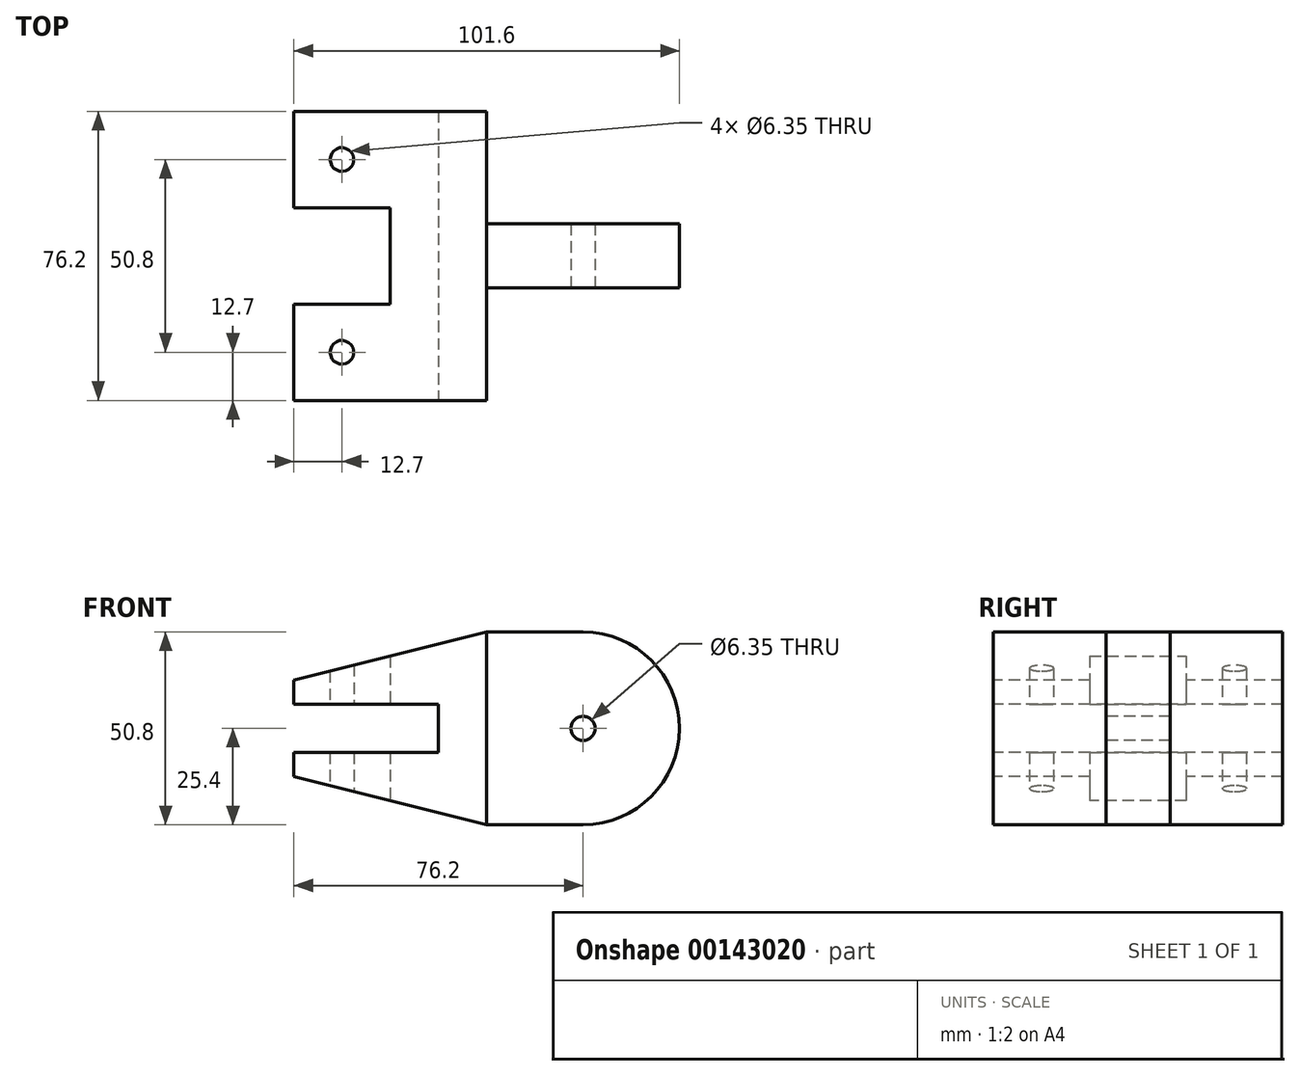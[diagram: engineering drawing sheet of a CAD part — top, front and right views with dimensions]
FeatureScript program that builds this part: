
annotation { "Feature Type Name" : "Feature", "Feature Type Description" : "" }
export const myFeature = defineFeature(function(context is Context, id is Id, definition is map)
    precondition{}
    {
        {
            var Q0;
            Q0=qCreatedBy(makeId("Top.planeOp"),FACE);
            var sketch = newSketch(context, id + "F0", { "sketchPlane" : qUnion([Q0])});
            skLineSegment(sketch, "E0.bottom", {"start": v(0, 0) * mm, "end": v(-50.8, 0) * mm});
            skLineSegment(sketch, "E0.top", {"start": v(0, 76.2) * mm, "end": v(-50.8, 76.2) * mm});
            skLineSegment(sketch, "E0.left", {"start": v(0, 0) * mm, "end": v(0, 76.2) * mm});
            skLineSegment(sketch, "E0.right", {"start": v(-50.8, 0) * mm, "end": v(-50.8, 25.4) * mm});
            skLineSegment(sketch, "E1.bottom", {"start": v(-50.8, 50.8) * mm, "end": v(-25.4, 50.8) * mm});
            skLineSegment(sketch, "E1.top", {"start": v(-50.8, 25.4) * mm, "end": v(-25.4, 25.4) * mm});
            skLineSegment(sketch, "E1.right", {"start": v(-25.4, 50.8) * mm, "end": v(-25.4, 25.4) * mm});
            skLineSegment(sketch, "E2.trimOffspring", {"start": v(-50.8, 50.8) * mm, "end": v(-50.8, 76.2) * mm});
            skLineSegment(sketch, "E3.bottom", {"start": v(0, 46.57) * mm, "end": v(50.8, 46.57) * mm});
            skLineSegment(sketch, "E3.top", {"start": v(0, 29.63) * mm, "end": v(50.8, 29.63) * mm});
            skLineSegment(sketch, "E3.left", {"start": v(0, 46.57) * mm, "end": v(0, 29.63) * mm});
            skLineSegment(sketch, "E3.right", {"start": v(50.8, 46.57) * mm, "end": v(50.8, 29.63) * mm});
            skSolve(sketch);
        }
        {
            var Q0;
            Q0=makeQuery(id+"F0.imprint","IMPRINT",FACE,{"disambiguationData":[TD([[makeQuery(id+"F0.imprint","IMPRINT",EDGE,{"derivedFrom":sQuery(id+"F0.wireOp",EDGE,"E0.bottom")}),-1.0]])]});
            var Q1;
            Q1=makeQuery(id+"F0.imprint","IMPRINT",FACE,{"disambiguationData":[TD([[makeQuery(id+"F0.imprint","IMPRINT",EDGE,{"derivedFrom":sQuery(id+"F0.wireOp",EDGE,"E3.bottom")}),-1.0]])]});
            extrude(context, id + "F1", {"entities" : qUnion([Q0, Q1]), "depth" : 50.8 * mm});
        }
        {
            var Q0;
            Q0=makeQuery(id+"F1.opExtrude","CAP_EDGE",EDGE,{"disambiguationData":[OSD([sQuery(id+"F0.wireOp",EDGE,"E3.right")])],"isStart":false});
            var Q1;
            Q1=makeQuery(id+"F1.opExtrude","CAP_EDGE",EDGE,{"disambiguationData":[OSD([sQuery(id+"F0.wireOp",EDGE,"E3.right")])],"isStart":true});
            fillet(context, id + "F2", {"entities" : qUnion([Q0, Q1]), "radius" : 25.4 * mm, "tangentPropagation" : true, "allowEdgeOverflow" : false});
        }
        {
            var Q0;
            Q0=makeQuery(id+"F1.opExtrude","SWEPT_FACE",FACE,{"disambiguationData":[OSD([sQuery(id+"F0.wireOp",EDGE,"E0.bottom")])]});
            var sketch = newSketch(context, id + "F3", { "sketchPlane" : qUnion([Q0])});
            skLineSegment(sketch, "E4", {"start": v(-50.8, 12.7) * mm, "end": v(-50.8, 0) * mm});
            skLineSegment(sketch, "E5", {"start": v(-50.8, 0) * mm, "end": v(0, 0) * mm});
            skLineSegment(sketch, "E6", {"start": v(0, 0) * mm, "end": v(-50.8, 12.7) * mm});
            skLineSegment(sketch, "E7", {"start": v(-50.8, 50.8) * mm, "end": v(-50.8, 38.1) * mm});
            skLineSegment(sketch, "E8", {"start": v(-50.8, 38.1) * mm, "end": v(0, 50.8) * mm});
            skLineSegment(sketch, "E9", {"start": v(0, 50.8) * mm, "end": v(-50.8, 50.8) * mm});
            skSolve(sketch);
        }
        {
            var Q0;
            Q0=makeQuery(id+"F3.imprint","IMPRINT",FACE,{"disambiguationData":[TD([[makeQuery(id+"F3.imprint","IMPRINT",EDGE,{"derivedFrom":sQuery(id+"F3.wireOp",EDGE,"E7")}),1.0]])]});
            var Q1;
            Q1=makeQuery(id+"F3.imprint","IMPRINT",FACE,{"disambiguationData":[TD([[makeQuery(id+"F3.imprint","IMPRINT",EDGE,{"derivedFrom":sQuery(id+"F3.wireOp",EDGE,"E4")}),1.0]])]});
            extrude(context, id + "F4", {"entities" : qUnion([Q0, Q1]), "operationType" : NewBodyOperationType.REMOVE, "oppositeDirection" : true, "depth" : 119.5 * mm});
        }
        {
            var Q0;
            Q0=makeQuery(id+"F1.opExtrude","SWEPT_FACE",FACE,{"disambiguationData":[OSD([sQuery(id+"F0.wireOp",EDGE,"E3.top")])]});
            var sketch = newSketch(context, id + "F5", { "sketchPlane" : qUnion([Q0])});
            skCircle(sketch, "E10", {"center": v(25.4, 25.4) * mm, "radius": 3.18 * mm});
            skSolve(sketch);
        }
        {
            var Q0;
            Q0=makeQuery(id+"F5.imprint","IMPRINT",FACE,{"disambiguationData":[TD([[makeQuery(id+"F5.imprint","IMPRINT",EDGE,{"derivedFrom":sQuery(id+"F5.wireOp",EDGE,"E10")}),1.0]])]});
            extrude(context, id + "F6", {"entities" : qUnion([Q0]), "operationType" : NewBodyOperationType.REMOVE, "oppositeDirection" : true, "depth" : 61.82 * mm});
        }
        {
            var Q0;
            {var subQ3=sQuery(id+"F0.wireOp",EDGE,"E0.bottom");Q0=makeQuery(id+"F0.imprint","IMPRINT",FACE,{"disambiguationData":[TD([[makeQuery(id+"F0.imprint","IMPRINT",EDGE,{"derivedFrom":subQ3}),-1.0]])]});}
            var sketch = newSketch(context, id + "F7", { "sketchPlane" : qUnion([Q0])});
            skCircle(sketch, "E11", {"center": v(-38.1, 12.7) * mm, "radius": 3.18 * mm});
            skCircle(sketch, "E12", {"center": v(-38.1, 63.5) * mm, "radius": 3.18 * mm});
            skSolve(sketch);
        }
        {
            var Q0;
            Q0=makeQuery(id+"F7.imprint","IMPRINT",FACE,{"disambiguationData":[TD([[makeQuery(id+"F7.imprint","IMPRINT",EDGE,{"derivedFrom":sQuery(id+"F7.wireOp",EDGE,"E11")}),1.0]])]});
            var Q1;
            Q1=makeQuery(id+"F7.imprint","IMPRINT",FACE,{"disambiguationData":[TD([[makeQuery(id+"F7.imprint","IMPRINT",EDGE,{"derivedFrom":sQuery(id+"F7.wireOp",EDGE,"E12")}),1.0]])]});
            extrude(context, id + "F8", {"entities" : qUnion([Q0, Q1]), "operationType" : NewBodyOperationType.REMOVE, "depth" : 63.5 * mm});
        }
        {
            var Q0;
            Q0=makeQuery(id+"F1.opExtrude","SWEPT_FACE",FACE,{"disambiguationData":[OSD([sQuery(id+"F0.wireOp",EDGE,"E0.bottom")])]});
            var sketch = newSketch(context, id + "F9", { "sketchPlane" : qUnion([Q0])});
            skLineSegment(sketch, "E13.bottom", {"start": v(-50.8, 19.05) * mm, "end": v(-12.7, 19.05) * mm});
            skLineSegment(sketch, "E13.top", {"start": v(-50.8, 31.75) * mm, "end": v(-12.7, 31.75) * mm});
            skLineSegment(sketch, "E13.left", {"start": v(-50.8, 19.05) * mm, "end": v(-50.8, 31.75) * mm});
            skLineSegment(sketch, "E13.right", {"start": v(-12.7, 19.05) * mm, "end": v(-12.7, 31.75) * mm});
            skSolve(sketch);
        }
        {
            var Q0;
            Q0=makeQuery(id+"F9.imprint","IMPRINT",FACE,{"disambiguationData":[TD([[makeQuery(id+"F9.imprint","IMPRINT",EDGE,{"derivedFrom":sQuery(id+"F9.wireOp",EDGE,"E13.bottom")}),1.0]])]});
            extrude(context, id + "F10", {"entities" : qUnion([Q0]), "operationType" : NewBodyOperationType.REMOVE, "oppositeDirection" : true, "depth" : 115 * mm});
        }
    });
